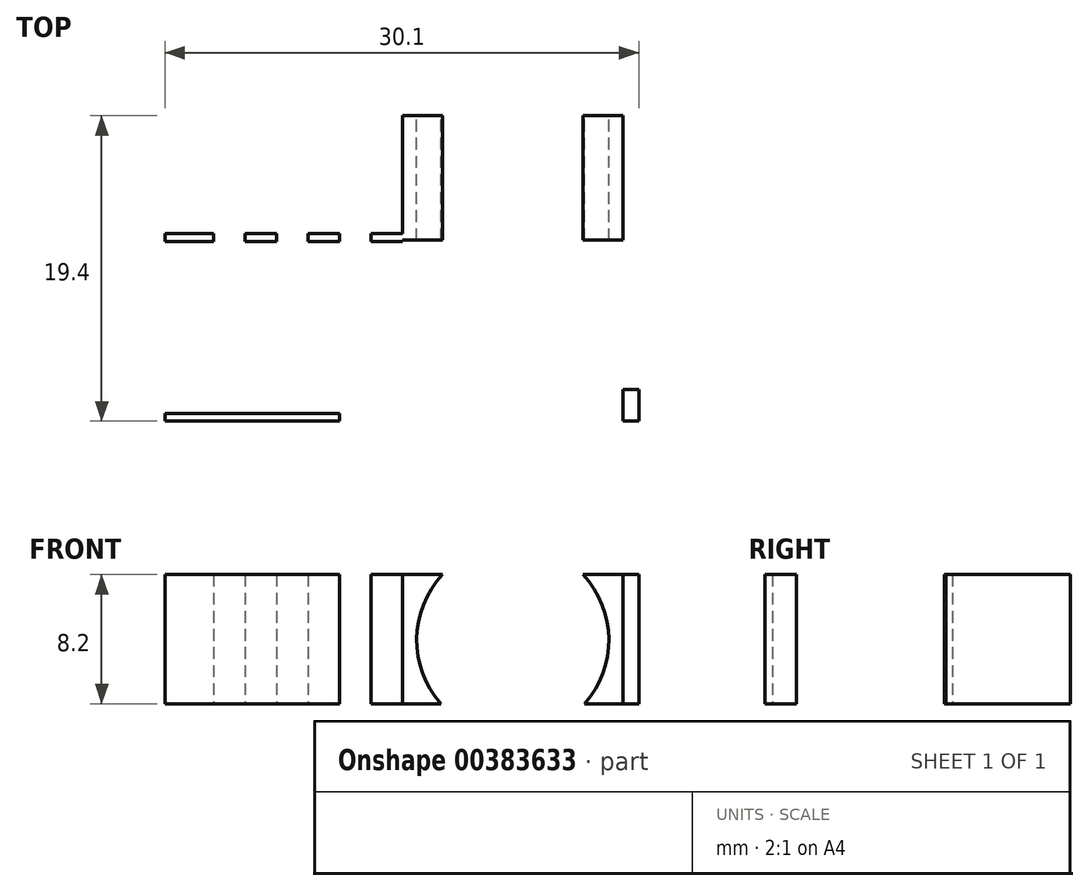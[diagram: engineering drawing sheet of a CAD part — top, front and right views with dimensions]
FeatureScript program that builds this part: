
annotation { "Feature Type Name" : "Feature", "Feature Type Description" : "" }
export const myFeature = defineFeature(function(context is Context, id is Id, definition is map)
    precondition{}
    {
        {
            var Q0;
            Q0=qCreatedBy(makeId("Top.planeOp"),FACE);
            var sketch = newSketch(context, id + "F0", { "sketchPlane" : qUnion([Q0])});
            skLineSegment(sketch, "E0.bottom", {"start": v(0, 0) * mm, "end": v(29.1, 0) * mm});
            skLineSegment(sketch, "E0.top", {"start": v(0, 11.4) * mm, "end": v(29.1, 11.4) * mm});
            skLineSegment(sketch, "E0.left", {"start": v(0, 0) * mm, "end": v(0, 11.4) * mm});
            skLineSegment(sketch, "E0.right", {"start": v(29.1, 0) * mm, "end": v(29.1, 11.4) * mm});
            skLineSegment(sketch, "E1.bottom", {"start": v(29.1, 11.4) * mm, "end": v(15.1, 11.4) * mm});
            skLineSegment(sketch, "E1.top", {"start": v(29.1, 25.4) * mm, "end": v(15.1, 25.4) * mm});
            skLineSegment(sketch, "E1.left", {"start": v(29.1, 11.4) * mm, "end": v(29.1, 25.4) * mm});
            skLineSegment(sketch, "E1.right", {"start": v(15.1, 11.4) * mm, "end": v(15.1, 25.4) * mm});
            skSolve(sketch);
        }
        {
            var Q0;
            Q0=qSketchRegion(id+"F0",true);
            extrude(context, id + "F1", {"entities" : qUnion([Q0]), "depth" : 8.2 * mm});
        }
        {
            var Q0;
            Q0=makeQuery(id+"F1.opExtrude","SWEPT_FACE",FACE,{"disambiguationData":[OSD([sQuery(id+"F0.wireOp",EDGE,"E0.bottom")])]});
            var sketch = newSketch(context, id + "F2", { "sketchPlane" : qUnion([Q0])});
            skLineSegment(sketch, "E2.bottom", {"start": v(29.1, 8.2) * mm, "end": v(11.1, 8.2) * mm});
            skLineSegment(sketch, "E2.top", {"start": v(29.1, 0) * mm, "end": v(11.1, 0) * mm});
            skLineSegment(sketch, "E2.left", {"start": v(29.1, 8.2) * mm, "end": v(29.1, 0) * mm});
            skLineSegment(sketch, "E2.right", {"start": v(11.1, 8.2) * mm, "end": v(11.1, 0) * mm});
            skLineSegment(sketch, "E3.bottom", {"start": v(11.1, 0) * mm, "end": v(29.1, 0) * mm});
            skLineSegment(sketch, "E3.top", {"start": v(11.1, 0.5) * mm, "end": v(29.1, 0.5) * mm});
            skLineSegment(sketch, "E3.left", {"start": v(11.1, 0) * mm, "end": v(11.1, 0.5) * mm});
            skLineSegment(sketch, "E3.right", {"start": v(29.1, 0) * mm, "end": v(29.1, 0.5) * mm});
            skLineSegment(sketch, "E4.bottom", {"start": v(11.1, 8.2) * mm, "end": v(29.1, 8.2) * mm});
            skLineSegment(sketch, "E4.top", {"start": v(11.1, 7.7) * mm, "end": v(29.1, 7.7) * mm});
            skLineSegment(sketch, "E4.left", {"start": v(11.1, 8.2) * mm, "end": v(11.1, 7.7) * mm});
            skLineSegment(sketch, "E4.right", {"start": v(29.1, 8.2) * mm, "end": v(29.1, 7.7) * mm});
            skSolve(sketch);
        }
        {
            var Q0;
            Q0=makeQuery(id+"F2.imprint","IMPRINT",FACE,{"disambiguationData":[TD([[makeQuery(id+"F2.imprint","IMPRINT",EDGE,{"derivedFrom":sQuery(id+"F2.wireOp",EDGE,"E2.left")}),-1.0]])]});
            extrude(context, id + "F3", {"entities" : qUnion([Q0]), "operationType" : NewBodyOperationType.REMOVE, "oppositeDirection" : true, "depth" : 11.5 * mm});
        }
        {
            var Q0;
            Q0=makeQuery(id+"F1.opExtrude","SWEPT_FACE",FACE,{"disambiguationData":[OSD([sQuery(id+"F0.wireOp",EDGE,"E1.top")])]});
            var sketch = newSketch(context, id + "F4", { "sketchPlane" : qUnion([Q0])});
            skCircle(sketch, "E5", {"center": v(-22.1, 4.05) * mm, "radius": 6.1 * mm});
            skSolve(sketch);
        }
        {
            var Q0;
            {var subQ0=sQuery(id+"F4.wireOp",EDGE,"E5");var subQ1=sQuery(id+"F0.wireOp",EDGE,"E1.top");var subQ2=makeQuery(id+"F1.opExtrude","CAP_EDGE",EDGE,{"disambiguationData":[OSD([subQ1])],"isStart":false});var subQ3=makeQuery(id+"F4.imprint","INTERSECT",VERTEX,{"disambiguationData":[OD(0.0)],"derivedFrom":[subQ2,subQ0]});Q0=makeQuery(id+"F4.imprint","IMPRINT",FACE,{"disambiguationData":[TD([[makeQuery(id+"F4.imprint","IMPRINT",EDGE,{"disambiguationData":[TD([[subQ3,-1.0]])],"derivedFrom":subQ0}),1.0]])]});}
            extrude(context, id + "F5", {"entities" : qUnion([Q0]), "operationType" : NewBodyOperationType.REMOVE, "oppositeDirection" : true, "depth" : 14 * mm});
        }
        {
            var Q0;
            Q0=makeQuery(id+"F1.opExtrude","SWEPT_FACE",FACE,{"disambiguationData":[OSD([sQuery(id+"F0.wireOp",EDGE,"E0.left")])]});
            var sketch = newSketch(context, id + "F6", { "sketchPlane" : qUnion([Q0])});
            skLineSegment(sketch, "E6.bottom", {"start": v(0, 8.2) * mm, "end": v(-0.5, 8.2) * mm});
            skLineSegment(sketch, "E6.top", {"start": v(0, 0) * mm, "end": v(-0.5, 0) * mm});
            skLineSegment(sketch, "E6.left", {"start": v(0, 8.2) * mm, "end": v(0, 0) * mm});
            skLineSegment(sketch, "E6.right", {"start": v(-0.5, 8.2) * mm, "end": v(-0.5, 0) * mm});
            skLineSegment(sketch, "E7.bottom", {"start": v(-11.4, 8.2) * mm, "end": v(-0.5, 8.2) * mm});
            skLineSegment(sketch, "E7.top", {"start": v(-11.4, 7.7) * mm, "end": v(-0.5, 7.7) * mm});
            skLineSegment(sketch, "E7.left", {"start": v(-11.4, 8.2) * mm, "end": v(-11.4, 7.7) * mm});
            skLineSegment(sketch, "E7.right", {"start": v(-0.5, 8.2) * mm, "end": v(-0.5, 7.7) * mm});
            skLineSegment(sketch, "E8.bottom", {"start": v(-11.4, 0) * mm, "end": v(-0.5, 0) * mm});
            skLineSegment(sketch, "E8.top", {"start": v(-11.4, 0.5) * mm, "end": v(-0.5, 0.5) * mm});
            skLineSegment(sketch, "E8.left", {"start": v(-11.4, 0) * mm, "end": v(-11.4, 0.5) * mm});
            skLineSegment(sketch, "E8.right", {"start": v(-0.5, 0) * mm, "end": v(-0.5, 0.5) * mm});
            skSolve(sketch);
        }
        {
            var Q0;
            {var subQ0=sQuery(id+"F6.wireOp",EDGE,"E6.right");Q0=makeQuery(id+"F6.imprint","IMPRINT",FACE,{"disambiguationData":[TD([[makeQuery(id+"F6.imprint","IMPRINT",EDGE,{"derivedFrom":subQ0}),-1.0]])]});}
            extrude(context, id + "F7", {"entities" : qUnion([Q0]), "operationType" : NewBodyOperationType.REMOVE, "oppositeDirection" : true, "depth" : 25 * mm});
        }
        {
            var Q0;
            Q0=qCreatedBy(makeId("Top.planeOp"),FACE);
            var sketch = newSketch(context, id + "F8", { "sketchPlane" : qUnion([Q0])});
            skLineSegment(sketch, "E9.bottom", {"start": v(0, 11.41) * mm, "end": v(15.1, 11.41) * mm});
            skLineSegment(sketch, "E9.top", {"start": v(0, 18.93) * mm, "end": v(15.1, 18.93) * mm});
            skLineSegment(sketch, "E9.left", {"start": v(0, 11.41) * mm, "end": v(0, 18.93) * mm});
            skLineSegment(sketch, "E9.right", {"start": v(15.1, 11.41) * mm, "end": v(15.1, 18.93) * mm});
            skSolve(sketch);
        }
        {
            var Q0;
            Q0=makeQuery(id+"F8.imprint","IMPRINT",FACE,{"disambiguationData":[TD([[makeQuery(id+"F8.imprint","IMPRINT",EDGE,{"derivedFrom":sQuery(id+"F8.wireOp",EDGE,"E9.bottom")}),1.0]])]});
            var Q1;
            Q1=qSketchRegion(id+"F8",true);
            extrude(context, id + "F9", {"entities" : qUnion([Q0, Q1]), "operationType" : NewBodyOperationType.ADD, "depth" : 8.2 * mm});
        }
        {
            var Q0;
            Q0=makeQuery(id+"F9.opExtrude","SWEPT_FACE",FACE,{"disambiguationData":[OSD([sQuery(id+"F8.wireOp",EDGE,"E9.top")])]});
            extrude(context, id + "F10", {"entities" : qUnion([Q0]), "operationType" : NewBodyOperationType.REMOVE, "oppositeDirection" : true, "depth" : 7 * mm});
        }
        {
            var Q0;
            Q0=makeQuery(id+"F10.boolean.opBoolean","COPY",FACE,{"derivedFrom":makeQuery(id+"F10.opExtrude","CAP_FACE",FACE,{"disambiguationData":[OSD([sQuery(id+"F8.wireOp",EDGE,"E9.top")])],"isStart":false})});
            var sketch = newSketch(context, id + "F11", { "sketchPlane" : qUnion([Q0])});
            skLineSegment(sketch, "E10.bottom", {"start": v(-15.1, 8.2) * mm, "end": v(-13.1, 8.2) * mm});
            skLineSegment(sketch, "E10.top", {"start": v(-15.1, 0) * mm, "end": v(-13.1, 0) * mm});
            skLineSegment(sketch, "E10.left", {"start": v(-15.1, 8.2) * mm, "end": v(-15.1, 0) * mm});
            skLineSegment(sketch, "E10.right", {"start": v(-13.1, 8.2) * mm, "end": v(-13.1, 0) * mm});
            skLineSegment(sketch, "E11.bottom", {"start": v(-13.1, 8.2) * mm, "end": v(-11.1, 8.2) * mm});
            skLineSegment(sketch, "E11.top", {"start": v(-13.1, 0) * mm, "end": v(-11.1, 0) * mm});
            skLineSegment(sketch, "E11.right", {"start": v(-11.1, 8.2) * mm, "end": v(-11.1, 0) * mm});
            skLineSegment(sketch, "E12.bottom", {"start": v(-11.1, 8.2) * mm, "end": v(-9.1, 8.2) * mm});
            skLineSegment(sketch, "E12.top", {"start": v(-11.1, 0) * mm, "end": v(-9.1, 0) * mm});
            skLineSegment(sketch, "E12.right", {"start": v(-9.1, 8.2) * mm, "end": v(-9.1, 0) * mm});
            skLineSegment(sketch, "E13.bottom", {"start": v(-9.1, 8.2) * mm, "end": v(-7.1, 8.2) * mm});
            skLineSegment(sketch, "E13.top", {"start": v(-9.1, 0) * mm, "end": v(-7.1, 0) * mm});
            skLineSegment(sketch, "E13.right", {"start": v(-7.1, 8.2) * mm, "end": v(-7.1, 0) * mm});
            skLineSegment(sketch, "E14.bottom", {"start": v(-7.1, 8.2) * mm, "end": v(-5.1, 8.2) * mm});
            skLineSegment(sketch, "E14.top", {"start": v(-7.1, 0) * mm, "end": v(-5.1, 0) * mm});
            skLineSegment(sketch, "E14.right", {"start": v(-5.1, 8.2) * mm, "end": v(-5.1, 0) * mm});
            skLineSegment(sketch, "E15.bottom", {"start": v(-5.1, 8.2) * mm, "end": v(-3.1, 8.2) * mm});
            skLineSegment(sketch, "E15.top", {"start": v(-5.1, 0) * mm, "end": v(-3.1, 0) * mm});
            skLineSegment(sketch, "E15.right", {"start": v(-3.1, 8.2) * mm, "end": v(-3.1, 0) * mm});
            skSolve(sketch);
        }
        {
            var Q0;
            Q0=makeQuery(id+"F11.imprint","IMPRINT",FACE,{"disambiguationData":[TD([[makeQuery(id+"F11.imprint","IMPRINT",EDGE,{"derivedFrom":sQuery(id+"F11.wireOp",EDGE,"E11.bottom")}),1.0]])]});
            var Q1;
            Q1=makeQuery(id+"F11.imprint","IMPRINT",FACE,{"disambiguationData":[TD([[makeQuery(id+"F11.imprint","IMPRINT",EDGE,{"derivedFrom":sQuery(id+"F11.wireOp",EDGE,"E13.bottom")}),1.0]])]});
            var Q2;
            Q2=makeQuery(id+"F11.imprint","IMPRINT",FACE,{"disambiguationData":[TD([[makeQuery(id+"F11.imprint","IMPRINT",EDGE,{"derivedFrom":sQuery(id+"F11.wireOp",EDGE,"E15.bottom")}),1.0]])]});
            extrude(context, id + "F12", {"entities" : qUnion([Q0, Q1, Q2]), "operationType" : NewBodyOperationType.REMOVE, "oppositeDirection" : true, "depth" : 1 * mm});
        }
        {
            var Q0;
            {var subQ0=sQuery(id+"F0.wireOp",EDGE,"E1.right");var subQ2=sQuery(id+"F0.wireOp",EDGE,"E1.top");Q0=makeQuery(id+"F5.boolean.opBoolean","SPLIT",FACE,{"disambiguationData":[TD([makeQuery(id+"F1.opExtrude","SWEPT_FACE",FACE,{"disambiguationData":[OSD([subQ0])]})])],"derivedFrom":makeQuery(id+"F1.opExtrude","SWEPT_FACE",FACE,{"disambiguationData":[OSD([subQ2])]})});}
            var Q1;
            {var subQ1=sQuery(id+"F0.wireOp",EDGE,"E1.left");var subQ2=sQuery(id+"F0.wireOp",EDGE,"E1.top");var subQ3=sQuery(id+"F0.wireOp",EDGE,"E0.right");Q1=makeQuery(id+"F5.boolean.opBoolean","SPLIT",FACE,{"disambiguationData":[TD([makeQuery(id+"F1.opExtrude","SWEPT_FACE",FACE,{"disambiguationData":[OSD([subQ3,subQ1])]})])],"derivedFrom":makeQuery(id+"F1.opExtrude","SWEPT_FACE",FACE,{"disambiguationData":[OSD([subQ2])]})});}
            extrude(context, id + "F13", {"entities" : qUnion([Q0, Q1]), "operationType" : NewBodyOperationType.REMOVE, "oppositeDirection" : true, "depth" : 6 * mm});
        }
        {
            var Q0;
            Q0=makeQuery(id+"F1.opExtrude","SWEPT_FACE",FACE,{"disambiguationData":[OSD([sQuery(id+"F0.wireOp",EDGE,"E0.right"),sQuery(id+"F0.wireOp",EDGE,"E1.left")])]});
            var sketch = newSketch(context, id + "F14", { "sketchPlane" : qUnion([Q0])});
            skLineSegment(sketch, "E16.bottom", {"start": v(0, 8.2) * mm, "end": v(2, 8.2) * mm});
            skLineSegment(sketch, "E16.top", {"start": v(0, 0) * mm, "end": v(2, 0) * mm});
            skLineSegment(sketch, "E16.left", {"start": v(0, 8.2) * mm, "end": v(0, 0) * mm});
            skLineSegment(sketch, "E16.right", {"start": v(2, 8.2) * mm, "end": v(2, 0) * mm});
            skSolve(sketch);
        }
        {
            var Q0;
            {var subQ0=sQuery(id+"F14.wireOp",EDGE,"E16.left");var subQ1=sQuery(id+"F2.wireOp",EDGE,"E2.left");var subQ2=makeQuery(id+"F3.boolean.opBoolean","COPY",EDGE,{"derivedFrom":makeQuery(id+"F3.opExtrude","SWEPT_EDGE",EDGE,{"disambiguationData":[OSD([subQ1,sQuery(id+"F2.wireOp",EDGE,"E4.top"),sQuery(id+"F2.wireOp",EDGE,"E4.right")])]})});var subQ3=makeQuery(id+"F14.imprint","INTERSECT",VERTEX,{"derivedFrom":[subQ2,subQ0]});Q0=makeQuery(id+"F14.imprint","IMPRINT",FACE,{"disambiguationData":[TD([[makeQuery(id+"F14.imprint","IMPRINT",EDGE,{"disambiguationData":[TD([[subQ3,-1.0]])],"derivedFrom":subQ0}),1.0]])]});}
            var Q1;
            {var subQ0=sQuery(id+"F14.wireOp",EDGE,"E16.bottom");Q1=makeQuery(id+"F14.imprint","IMPRINT",FACE,{"disambiguationData":[TD([[makeQuery(id+"F14.imprint","IMPRINT",EDGE,{"derivedFrom":subQ0}),-1.0]])]});}
            var Q2;
            {var subQ0=sQuery(id+"F14.wireOp",EDGE,"E16.top");Q2=makeQuery(id+"F14.imprint","IMPRINT",FACE,{"disambiguationData":[TD([[makeQuery(id+"F14.imprint","IMPRINT",EDGE,{"derivedFrom":subQ0}),1.0]])]});}
            extrude(context, id + "F15", {"entities" : qUnion([Q0, Q1, Q2]), "operationType" : NewBodyOperationType.ADD, "depth" : 1 * mm});
        }
    });
